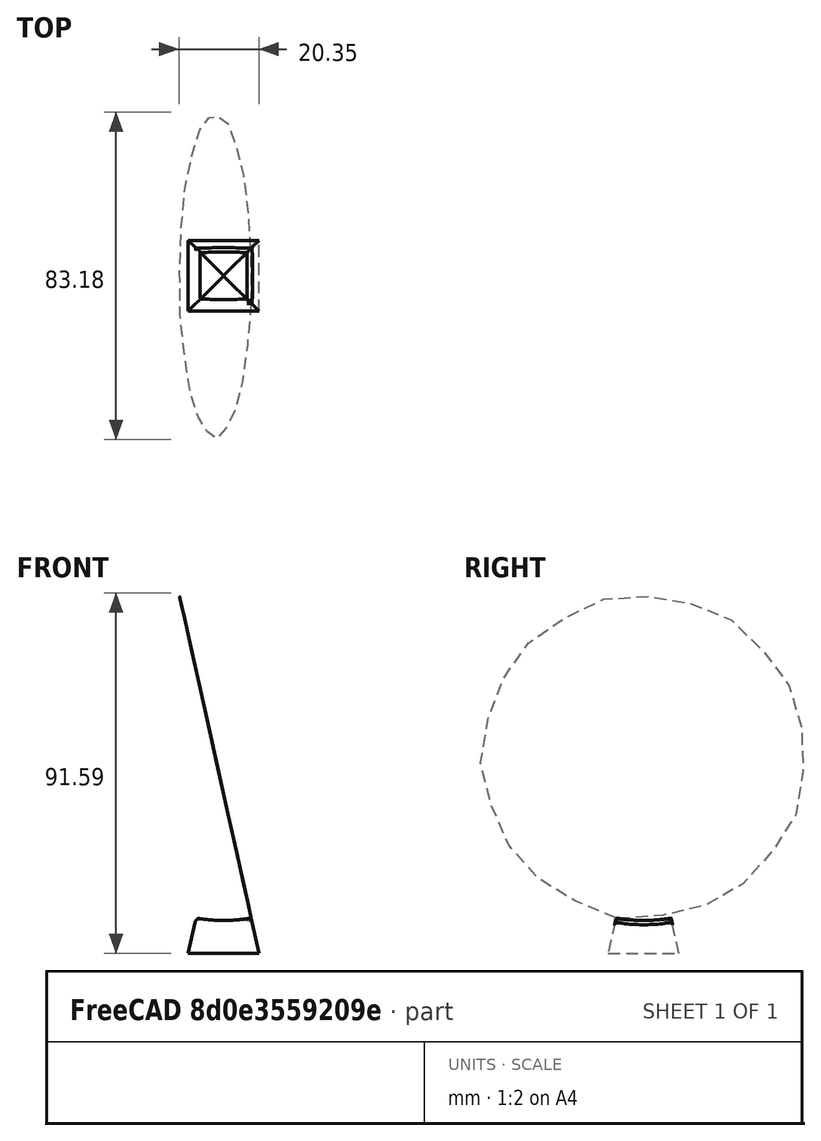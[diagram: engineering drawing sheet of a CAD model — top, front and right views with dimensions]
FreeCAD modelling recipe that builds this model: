
FCSTD DOCUMENT  (FreeCAD 0.20R)
Label: keycap_1U
License: All rights reserved
LicenseURL: http://en.wikipedia.org/wiki/All_rights_reserved
objects: Sketcher::SketchObject×2, Part::Extrusion×2, Part::MultiCommon×1, Part::Fillet×1
note: 6 computed .brp shape members not serialized (recipe doc carries the construction recipe); baked Part::Feature solids carry a one-line shape summary decoded from their .brp

FEATURE [Sketcher::SketchObject] Sketch001  label="Sketch2"
  FullyConstrained = false
  Placement = pos=(0,0,0) rot=(0.57735,0.57735,0.57735;2.0944rad)
  sketch-geometry (4):
    g0: LineSegment StartX=-7.00002 StartY=9 StartZ=0 EndX=-9 EndY=0 EndZ=0
    g1: LineSegment StartX=-9 StartY=0 StartZ=0 EndX=9 EndY=0 EndZ=0
    g2: LineSegment StartX=9 StartY=0 StartZ=0 EndX=7 EndY=9 EndZ=0
    g3: ArcOfCircle CenterX=0 CenterY=50 CenterZ=0 NormalX=0 NormalY=0 NormalZ=1 AngleXU=0 Radius=41.5933 StartAngle=4.54329 EndAngle=4.88149
  constraints (7):
    c: PointOnObject(g0,g-1)
    c: Coincident(g0,g1)
    c: PointOnObject(g1,g-1)
    c: Coincident(g1,g2)
    c: PointOnObject(g3,g-2)
    c: Coincident(g3,g0)
    c: Coincident(g3,g2)
FEATURE [Sketcher::SketchObject] Sketch  label="Sketch1"
  FullyConstrained = false
  Placement = pos=(0,0,0) rot=(1,0,0;1.5708rad)
  sketch-geometry (4):
    g0: LineSegment StartX=-7.00002 StartY=9 StartZ=0 EndX=-9 EndY=0 EndZ=0
    g1: LineSegment StartX=-9 StartY=0 StartZ=0 EndX=9 EndY=0 EndZ=0
    g2: LineSegment StartX=9 StartY=0 StartZ=0 EndX=7 EndY=9 EndZ=0
    g3: ArcOfCircle CenterX=0 CenterY=50 CenterZ=0 NormalX=0 NormalY=0 NormalZ=1 AngleXU=0 Radius=41.5933 StartAngle=4.54329 EndAngle=4.88149
  constraints (7):
    c: PointOnObject(g0,g-1)
    c: Coincident(g0,g1)
    c: PointOnObject(g1,g-1)
    c: Coincident(g1,g2)
    c: PointOnObject(g3,g-2)
    c: Coincident(g3,g0)
    c: Coincident(g3,g2)
FEATURE [Part::Extrusion] Extrude
  Base = -> Sketch001
  Dir = (1,0,0)
  DirMode = 2
  FaceMakerClass = Part::FaceMakerBullseye
  LengthFwd = 18
  LengthRev = 0
  Solid = true
  Symmetric = true
FEATURE [Part::Extrusion] Extrude001
  Base = -> Sketch
  Dir = (0,-1,-3e-16)
  DirMode = 2
  FaceMakerClass = Part::FaceMakerBullseye
  LengthFwd = 18
  LengthRev = 0
  Solid = true
  Symmetric = true
FEATURE [Part::MultiCommon] Common
  Shapes = -> [Extrude,Extrude001]
FEATURE [Part::Fillet] Fillet
  Base = -> Common
  Edges = 4 edges r=1.4: [Edge4,Edge5,Edge11,Edge17]
